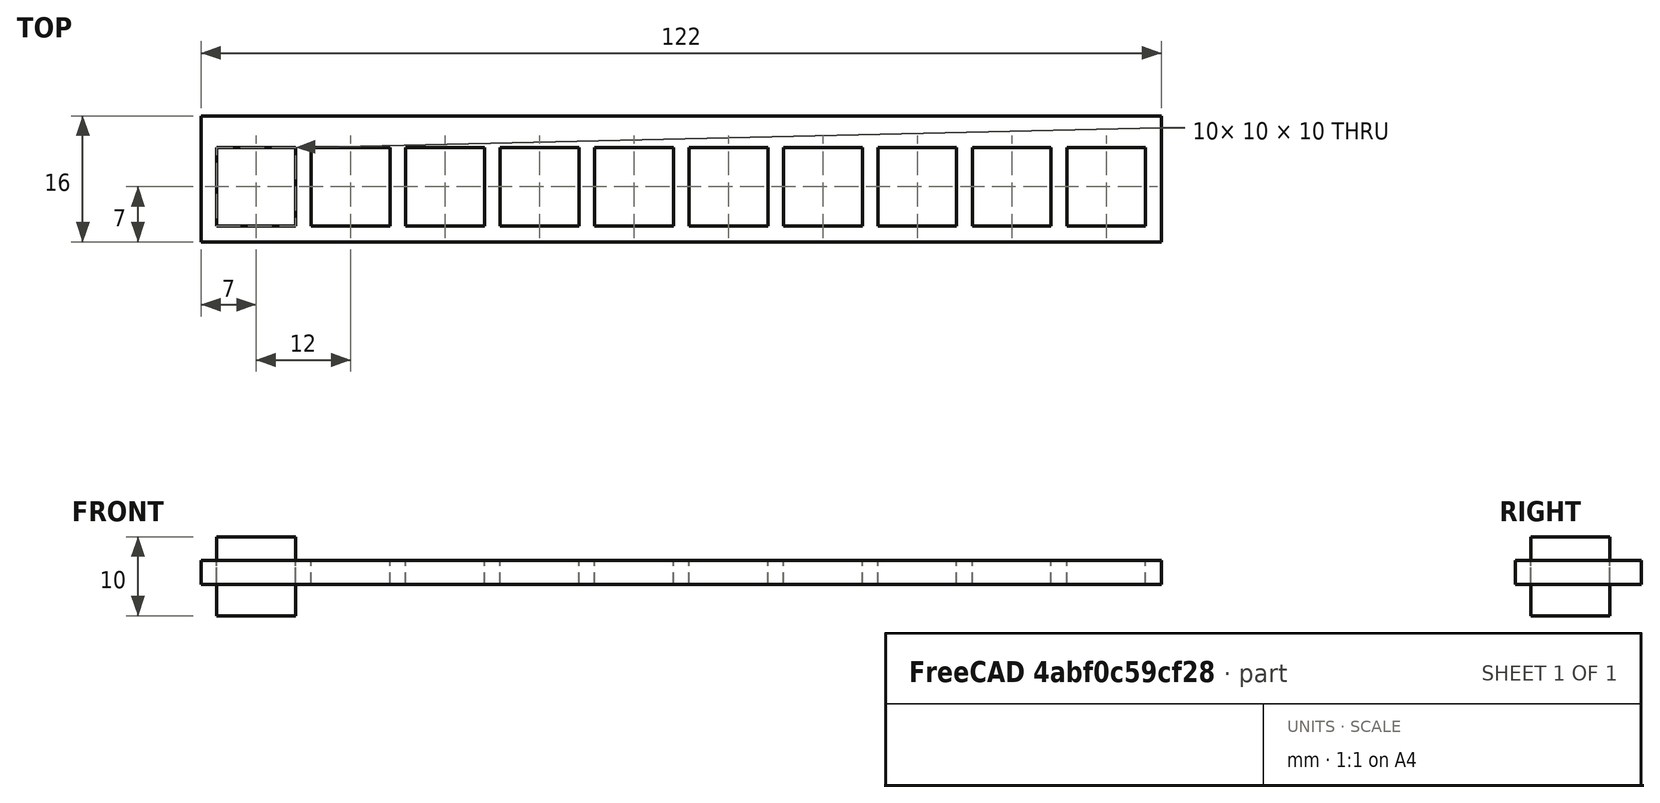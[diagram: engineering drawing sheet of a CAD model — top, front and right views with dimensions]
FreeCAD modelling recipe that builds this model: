
FCSTD DOCUMENT  (FreeCAD 0.21R33694 (Git))
Label: OJT1_T10P01_escala
License: All rights reserved
LicenseURL: http://en.wikipedia.org/wiki/All_rights_reserved
objects: Part::Box×2, Part::FeaturePython×1, Part::Cut×1
note: 3 computed .brp shape members not serialized (recipe doc carries the construction recipe); baked Part::Feature solids carry a one-line shape summary decoded from their .brp

FEATURE [Part::Box] Box  label="Cube"
  AttacherType = Attacher::AttachEngine3D
  Height = 10
  Length = 10
  Width = 10
FEATURE [Part::FeaturePython] Array  # Draft array (typed FeaturePython)
  AlwaysSyncPlacement = false
  Angle = 360
  ArrayType = 0
  Axis = (0,0,1)
  Base = -> Box
  Center = (0,0,0)
  Count = 10
  ExpandArray = false
  Fuse = false
  IntervalAxis = (0,0,0)
  IntervalX = (12,0,0)
  IntervalY = (0,100,0)
  IntervalZ = (0,0,100)
  NumberCircles = 3
  NumberPolar = 5
  NumberX = 10
  NumberY = 1
  NumberZ = 1
  PlacementList = 10 placements: arithmetic series from (0,0,0) step (12,0,0) to (108,0,0)
  RadialDistance = 50
  ScaleList = (10) [(1,1,1),(1,1,1),(1,1,1),(1,1,1),(1,1,1),(1,1,1),(1,1,1),(1,1,1),(1,1,1),(1,1,1)]
  Symmetry = 1
  TangentialDistance = 25
FEATURE [Part::Box] Box001  label="Cube001"
  AttacherType = Attacher::AttachEngine3D
  Height = 3
  Length = 122
  Placement = pos=(-2,-2,4) rot=(0,0,1;0rad)
  Width = 16
FEATURE [Part::Cut] Cut  label="escala"
  Base = -> Box001
  Refine = true
  Tool = -> Array
